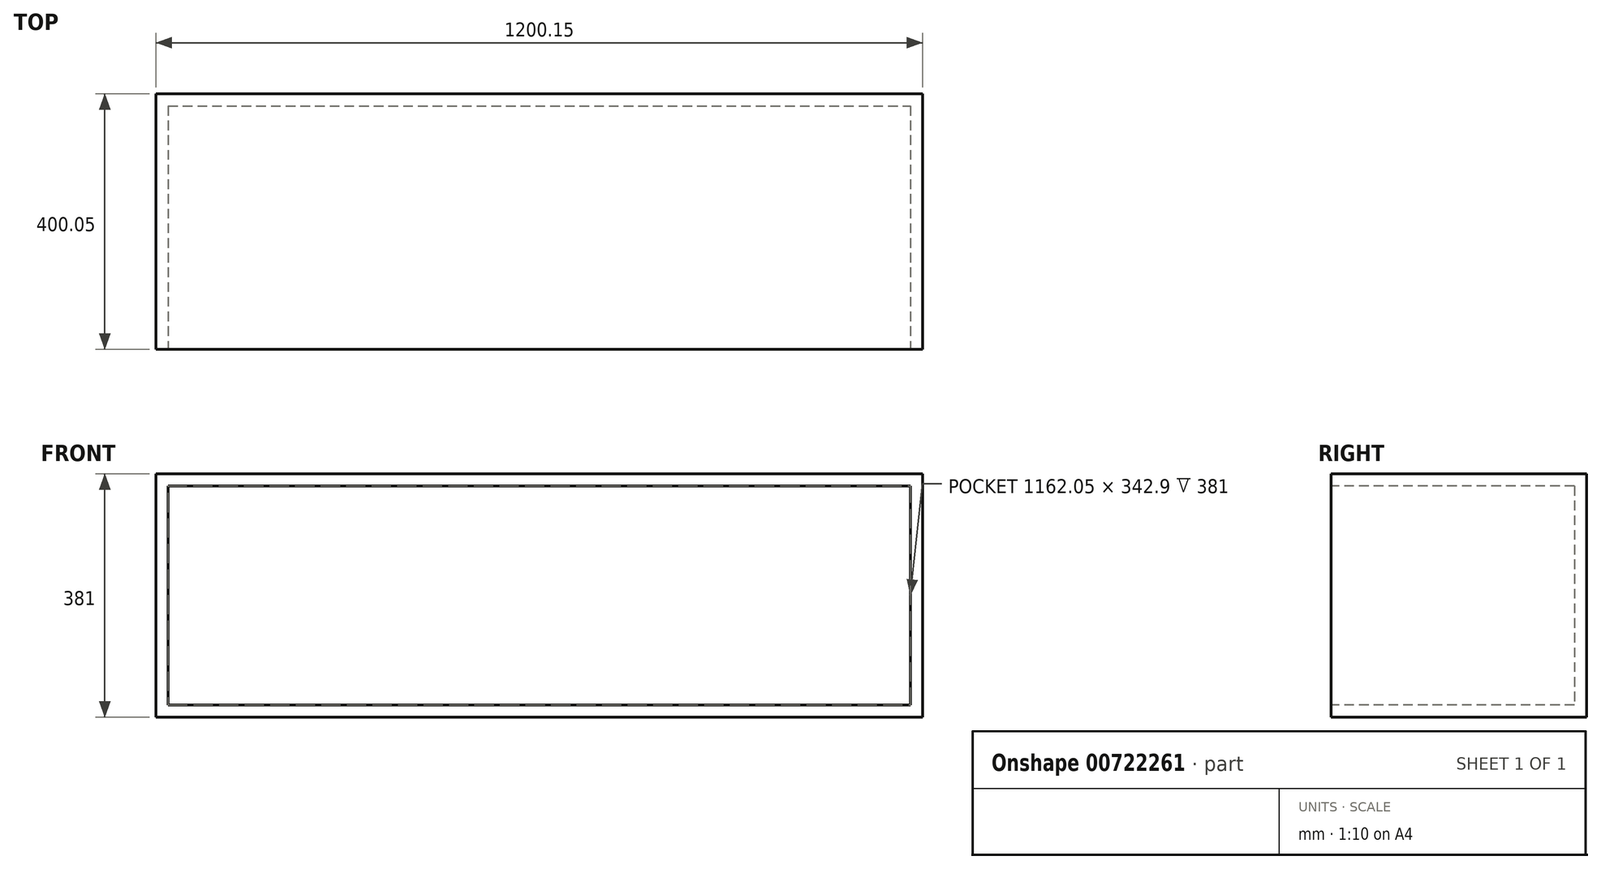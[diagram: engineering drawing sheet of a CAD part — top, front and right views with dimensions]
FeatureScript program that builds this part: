
annotation { "Feature Type Name" : "Feature", "Feature Type Description" : "" }
export const myFeature = defineFeature(function(context is Context, id is Id, definition is map)
    precondition{}
    {
        {
            var Q0;
            Q0=qCreatedBy(makeId("Front.planeOp"),FACE);
            var sketch = newSketch(context, id + "F0", { "sketchPlane" : qUnion([Q0])});
            skLineSegment(sketch, "E0.bottom", {"start": v(0, 0) * mm, "end": v(1200.15, 0) * mm});
            skLineSegment(sketch, "E0.top", {"start": v(0, -381) * mm, "end": v(1200.15, -381) * mm});
            skLineSegment(sketch, "E0.left", {"start": v(0, 0) * mm, "end": v(0, -381) * mm});
            skLineSegment(sketch, "E0.right", {"start": v(1200.15, 0) * mm, "end": v(1200.15, -381) * mm});
            skSolve(sketch);
        }
        {
            var Q0;
            Q0 = qSketchRegion(id + "F0", true);
            extrude(context, id + "F1", {"entities" : qUnion([Q0]), "oppositeDirection" : true, "depth" : 400.05 * mm, "offsetDistance" : 25.4 * mm});
        }
        {
            var Q0;
            Q0=makeQuery(id+"F1.opExtrude","CAP_FACE",FACE,{"disambiguationData":[OSD([sQuery(id+"F0.wireOp",EDGE,"E0.bottom"),sQuery(id+"F0.wireOp",EDGE,"E0.top"),sQuery(id+"F0.wireOp",EDGE,"E0.left"),sQuery(id+"F0.wireOp",EDGE,"E0.right")])],"isStart":true});
            shell(context, id + "F2", {"entities" : qUnion([Q0]), "thickness" : 19.05 * mm});
        }
    });
